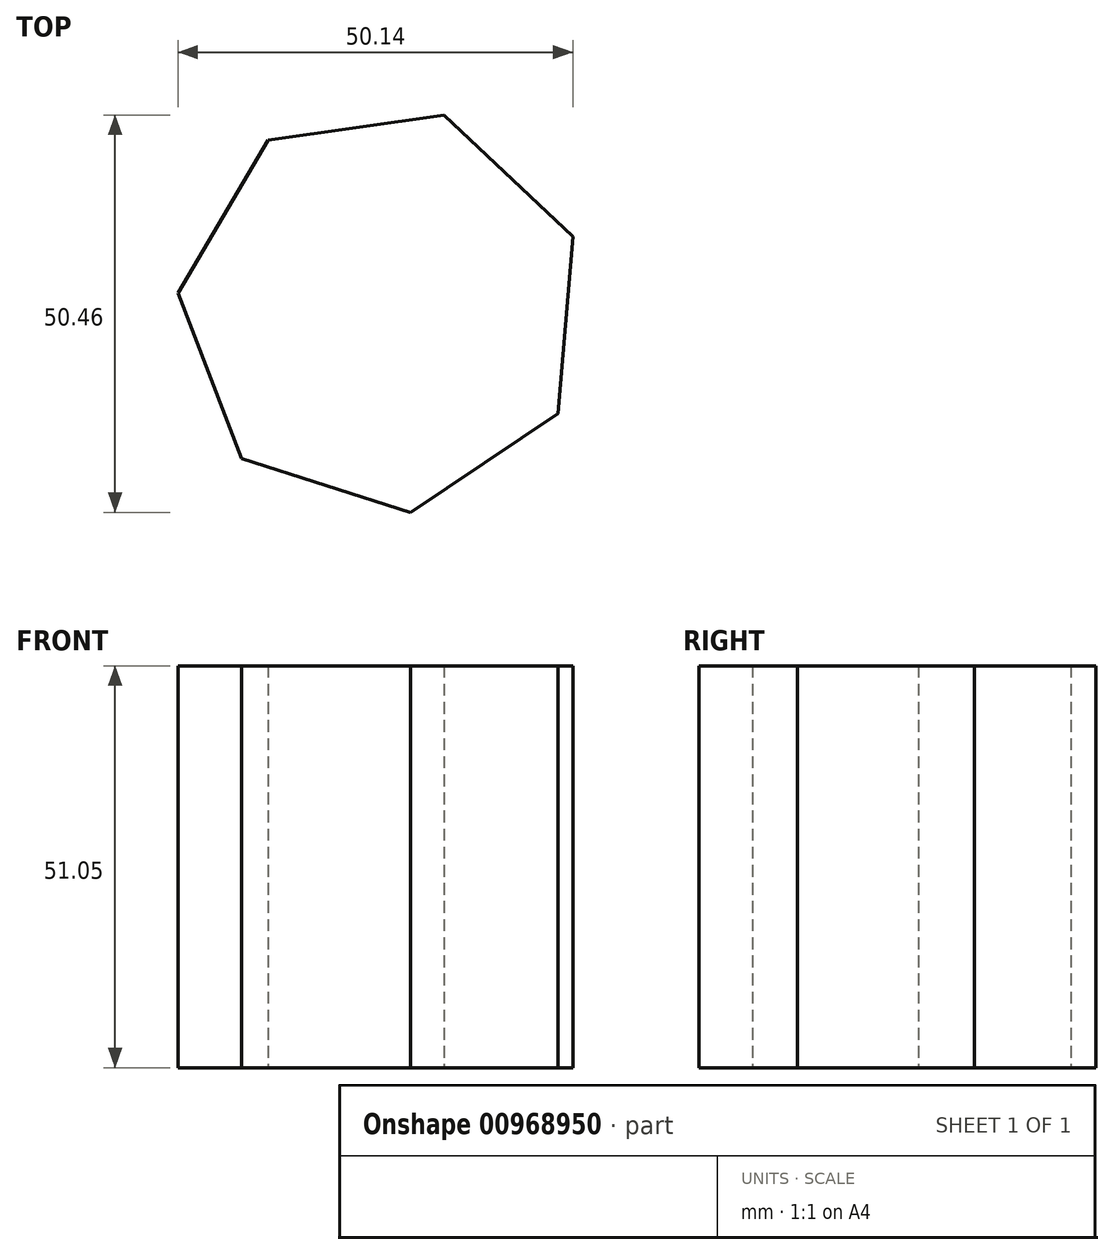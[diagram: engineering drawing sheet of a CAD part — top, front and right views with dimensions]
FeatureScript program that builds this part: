
annotation { "Feature Type Name" : "Feature", "Feature Type Description" : "" }
export const myFeature = defineFeature(function(context is Context, id is Id, definition is map)
    precondition{}
    {
        {
            var Q0;
            Q0=qCreatedBy(makeId("Top.planeOp"),FACE);
            var sketch = newSketch(context, id + "F0", { "sketchPlane" : qUnion([Q0])});
            skCircle(sketch, "E0.cCircle", {"center": v(105.45, 49.87) * mm, "radius": 23.4 * mm, "construction": true});
            skLineSegment(sketch, "E0.0", {"start": v(127.83, 36.7) * mm, "end": v(109.1, 24.16) * mm});
            skLineSegment(sketch, "E0.1", {"start": v(109.1, 24.16) * mm, "end": v(87.62, 30.98) * mm});
            skLineSegment(sketch, "E0.2", {"start": v(87.62, 30.98) * mm, "end": v(79.56, 52.02) * mm});
            skLineSegment(sketch, "E0.3", {"start": v(79.56, 52.02) * mm, "end": v(91, 71.45) * mm});
            skLineSegment(sketch, "E0.4", {"start": v(91, 71.45) * mm, "end": v(113.3, 74.62) * mm});
            skLineSegment(sketch, "E0.5", {"start": v(113.3, 74.62) * mm, "end": v(129.7, 59.16) * mm});
            skLineSegment(sketch, "E0.6", {"start": v(129.7, 59.16) * mm, "end": v(127.83, 36.7) * mm});
            skPoint(sketch, "E0.0.midPoint", {"position": v(118.47, 30.43) * mm});
            skSolve(sketch);
        }
        {
            var Q0;
            Q0 = qSketchRegion(id + "F0", true);
            extrude(context, id + "F1", {"entities" : qUnion([Q0]), "flatOperationType" : FlatOperationType.REMOVE, "depth" : 51.05 * mm, "offsetDistance" : 25.4 * mm, "domain" : OperationDomain.MODEL});
        }
    });
